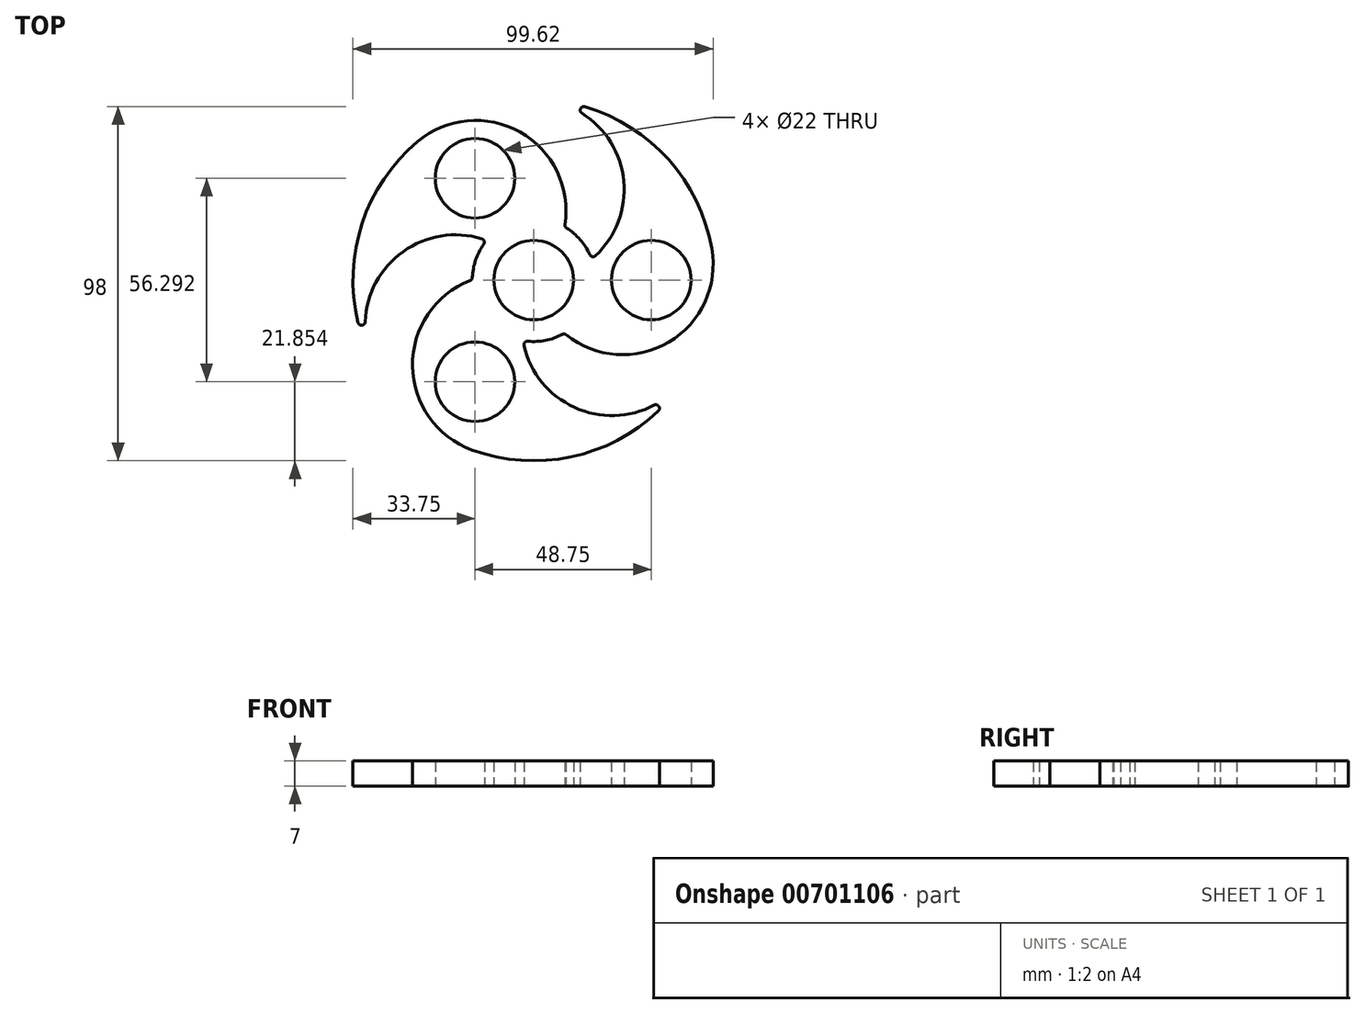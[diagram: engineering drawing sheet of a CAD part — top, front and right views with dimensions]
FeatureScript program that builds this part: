
annotation { "Feature Type Name" : "Feature", "Feature Type Description" : "" }
export const myFeature = defineFeature(function(context is Context, id is Id, definition is map)
    precondition{}
    {
        {
            var Q0;
            Q0=qCreatedBy(makeId("Top.planeOp"),FACE);
            var sketch = newSketch(context, id + "F0", { "sketchPlane" : qUnion([Q0])});
            skArc(sketch, "E0", {"start": v(49.24, 8.68) * mm, "mid": v(37.28, 33.32) * mm, "end": v(14.14, 47.96) * mm});
            skLineSegment(sketch, "E1", {"start": v(0, 0) * mm, "end": v(0, 11) * mm});
            skArc(sketch, "E2", {"start": v(-10.73, 2.42) * mm, "mid": v(0, 0) * mm, "end": v(10.73, 2.42) * mm});
            skArc(sketch, "E3.1.0", {"start": v(3.27, -10.5) * mm, "mid": v(0, 0) * mm, "end": v(-7.46, 8.08) * mm});
            skArc(sketch, "E3.2.0", {"start": v(7.46, 8.08) * mm, "mid": v(0, 0) * mm, "end": v(-3.27, -10.5) * mm});
            skCircle(sketch, "E4", {"center": v(0, 0) * mm, "radius": 11 * mm});
            skArc(sketch, "E5", {"start": v(-13.84, 9.88) * mm, "mid": v(-16.08, 5.51) * mm, "end": v(-16.99, 0.7) * mm});
            skLineSegment(sketch, "E6", {"start": v(0, 0) * mm, "end": v(10.83, 1.91) * mm});
            skArc(sketch, "E7", {"start": v(0.52, 10.99) * mm, "mid": v(0, 0) * mm, "end": v(4.25, -10.15) * mm});
            skArc(sketch, "E8.1.0", {"start": v(-9.78, -5.04) * mm, "mid": v(0, 0) * mm, "end": v(6.66, 8.75) * mm});
            skArc(sketch, "E8.2.0", {"start": v(9.26, -5.94) * mm, "mid": v(0, 0) * mm, "end": v(-10.91, 1.4) * mm});
            skPoint(sketch, "E9.orphan", {"position": v(49.24, 8.68) * mm});
            skArc(sketch, "E10.trimOffspring", {"start": v(-17.1, -46.98) * mm, "mid": v(10.21, -48.95) * mm, "end": v(34.46, -36.22) * mm});
            skArc(sketch, "E11.trimOffspring", {"start": v(-32.14, 38.3) * mm, "mid": v(-47.5, 15.63) * mm, "end": v(-48.6, -11.73) * mm});
            skArc(sketch, "E12.trimOffspring", {"start": v(8.64, 15.36) * mm, "mid": v(-3.81, 40.94) * mm, "end": v(-32.14, 38.3) * mm});
            skArc(sketch, "E13.trimOffspring", {"start": v(17.06, 6.73) * mm, "mid": v(24.89, 27.36) * mm, "end": v(13.32, 46.15) * mm});
            skArc(sketch, "E14.trimOffspring", {"start": v(8.98, -15.16) * mm, "mid": v(37.36, -17.17) * mm, "end": v(49.24, 8.68) * mm});
            skArc(sketch, "E15.trimOffspring", {"start": v(-2.7, -18.14) * mm, "mid": v(11.25, -35.23) * mm, "end": v(33.3, -34.62) * mm});
            skArc(sketch, "E16.trimOffspring", {"start": v(-17.62, -0.2) * mm, "mid": v(-33.55, -23.77) * mm, "end": v(-17.1, -46.98) * mm});
            skArc(sketch, "E17.trimOffspring", {"start": v(-14.36, 11.41) * mm, "mid": v(-36.14, 7.87) * mm, "end": v(-46.63, -11.54) * mm});
            skArc(sketch, "E18.trimOffspring", {"start": v(-1.63, -16.92) * mm, "mid": v(3.26, -16.68) * mm, "end": v(7.9, -15.06) * mm});
            skArc(sketch, "E19.trimOffspring", {"start": v(15.47, 7.05) * mm, "mid": v(12.82, 11.17) * mm, "end": v(9.1, 14.36) * mm});
            skLineSegment(sketch, "E20", {"start": v(0, 0) * mm, "end": v(-25, 43.3) * mm});
            skCircle(sketch, "E21", {"center": v(-16.25, 28.15) * mm, "radius": 11 * mm});
            skCircle(sketch, "E22.1.0", {"center": v(-16.25, -28.15) * mm, "radius": 11 * mm});
            skCircle(sketch, "E22.2.0", {"center": v(32.5, 0) * mm, "radius": 11 * mm});
            skPoint(sketch, "E23.visualSharp", {"position": v(-43.3, -25) * mm});
            skArc(sketch, "E23.filletArc", {"start": v(-48.6, -11.73) * mm, "mid": v(-47.53, -12.5) * mm, "end": v(-46.63, -11.54) * mm});
            skPoint(sketch, "E24.visualSharp", {"position": v(0, 50) * mm});
            skArc(sketch, "E24.filletArc", {"start": v(14.14, 47.96) * mm, "mid": v(12.95, 47.41) * mm, "end": v(13.32, 46.15) * mm});
            skPoint(sketch, "E25.visualSharp", {"position": v(43.3, -25) * mm});
            skArc(sketch, "E25.filletArc", {"start": v(34.46, -36.22) * mm, "mid": v(34.59, -34.92) * mm, "end": v(33.3, -34.62) * mm});
            skPoint(sketch, "E26.visualSharp", {"position": v(-2.99, -16.74) * mm});
            skArc(sketch, "E26.filletArc", {"start": v(-1.63, -16.92) * mm, "mid": v(-2.48, -17.26) * mm, "end": v(-2.7, -18.14) * mm});
            skPoint(sketch, "E27.visualSharp", {"position": v(8.47, -14.74) * mm});
            skArc(sketch, "E27.filletArc", {"start": v(8.98, -15.16) * mm, "mid": v(8.45, -14.95) * mm, "end": v(7.9, -15.06) * mm});
            skPoint(sketch, "E28.visualSharp", {"position": v(15.99, 5.78) * mm});
            skArc(sketch, "E28.filletArc", {"start": v(15.47, 7.05) * mm, "mid": v(16.19, 6.48) * mm, "end": v(17.06, 6.73) * mm});
            skPoint(sketch, "E29.visualSharp", {"position": v(8.53, 14.7) * mm});
            skArc(sketch, "E29.filletArc", {"start": v(8.64, 15.36) * mm, "mid": v(8.72, 14.8) * mm, "end": v(9.1, 14.36) * mm});
            skPoint(sketch, "E30.visualSharp", {"position": v(-13, 10.96) * mm});
            skArc(sketch, "E30.filletArc", {"start": v(-13.84, 9.88) * mm, "mid": v(-13.7, 10.78) * mm, "end": v(-14.36, 11.41) * mm});
            skPoint(sketch, "E31.visualSharp", {"position": v(-17, 0.04) * mm});
            skArc(sketch, "E31.filletArc", {"start": v(-17.62, -0.2) * mm, "mid": v(-17.17, 0.15) * mm, "end": v(-16.99, 0.7) * mm});
            skSolve(sketch);
        }
        {
            var Q0;
            Q0=qSketchRegion(id+"F0",true);
            extrude(context, id + "F1", {"entities" : qUnion([Q0]), "depth" : 7 * mm, "offsetDistance" : 25 * mm});
        }
    });
